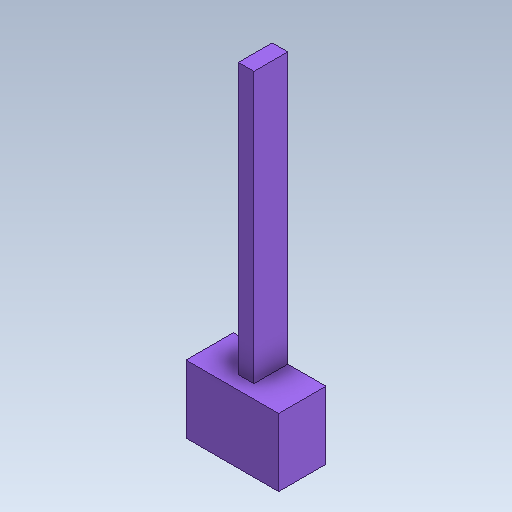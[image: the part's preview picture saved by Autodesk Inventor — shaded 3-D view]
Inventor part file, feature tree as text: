
AUTODESK INVENTOR PART (.ipt)
format: ipt  version: 2020 (Build 240168000, 168)  size: 259,584 bytes
history: native  units: in
note: dims shown in document units (in); Inventor stores cm internally (conversion verified against a paired STEP export)
features: extrude x13, sketch x13, projected_geometry x12
ambient origin geometry x8: Origin, YZ Plane, XZ Plane, XY Plane, X Axis, Y Axis, Z Axis, Center Point
bodies: Solid1 (feature_tree)
feature tree (38):
  extrude  "Extrusion1"  Depth=0.7874in
  extrude  "Extrusion4"  Depth=0.2894in
  extrude  "Extrusion5"  Depth=0.1378in TaperAngle=0.0deg
  extrude  "Extrusion6"  Depth=0.0797in
  extrude  "Extrusion7"  Depth=0.1575in
  extrude  "Extrusion8"  Depth=0.0787in TaperAngle=0.0deg
  extrude  "Extrusion9"  Depth=0.0394in
  extrude  "Extrusion10"  Depth=0.0689in TaperAngle=0.0deg
  extrude  "Extrusion11"  Depth=0.3937in TaperAngle=0.0deg
  extrude  "Extrusion12"  Depth=0.3937in TaperAngle=0.0deg
  extrude  "Extrusion17"  Depth=0.3937in TaperAngle=0.0deg
  extrude  "Extrusion18"  Depth=0.0039in
  extrude  "Extrusion19"  Depth=0.0394in TaperAngle=0.0deg
  sketch  "Sketch1"  dims[d0=0.7874in d1=0.1358in]
  sketch  "Sketch4"  dims[d2=0.1457in d3=0.2894in]
  projected_geometry  "Projected Loop3"
  sketch  "Sketch5"  dims[d4=0.1969in d5=0.1378in d6=0.0in]
  projected_geometry  "Projected Loop4"
  sketch  "Sketch6"  dims[d22=0.0797in d23=0.0797in]
  projected_geometry  "Projected Loop5"
  sketch  "Sketch7"  dims[d24=0.2953in d25=0.1575in]
  projected_geometry  "Projected Loop6"
  sketch  "Sketch8"  dims[d26=0.122in d27=0.0787in d28=0.0in]
  projected_geometry  "Projected Loop7"
  sketch  "Sketch9"  dims[d29=0.0394in d30=0.0394in]
  projected_geometry  "Projected Loop8"
  sketch  "Sketch10"  dims[d31=0.3937in d32=0.0in d33=0.0689in d34=0.0in]
  projected_geometry  "Projected Loop9"
  sketch  "Sketch11"  dims[d35=0.0197in d36=0.3937in d37=0.0in]
  projected_geometry  "Projected Loop10"
  sketch  "Sketch12"  dims[d38=0.0787in d39=0.0in d40=0.3937in d41=0.0in]
  projected_geometry  "Projected Loop11"
  sketch  "Sketch17"  dims[d42=0.3937in d43=0.0in d44=0.3937in d45=0.0in]
  projected_geometry  "Projected Loop16"
  sketch  "Sketch18"  dims[d46=0.3937in d47=0.0in d48=0.0039in]
  projected_geometry  "Projected Loop17"
  sketch  "Sketch19"  dims[d49=0.0039in d50=0.3937in d51=0.0in d63=0.0394in d64=0.0in d65=0.0059in d66=0.0059in d67=0.0394in d68=0.0in d69=0.0059in d70=0.0059in d71=0.0394in d72=0.0in]
  projected_geometry  "Projected Loop18"
